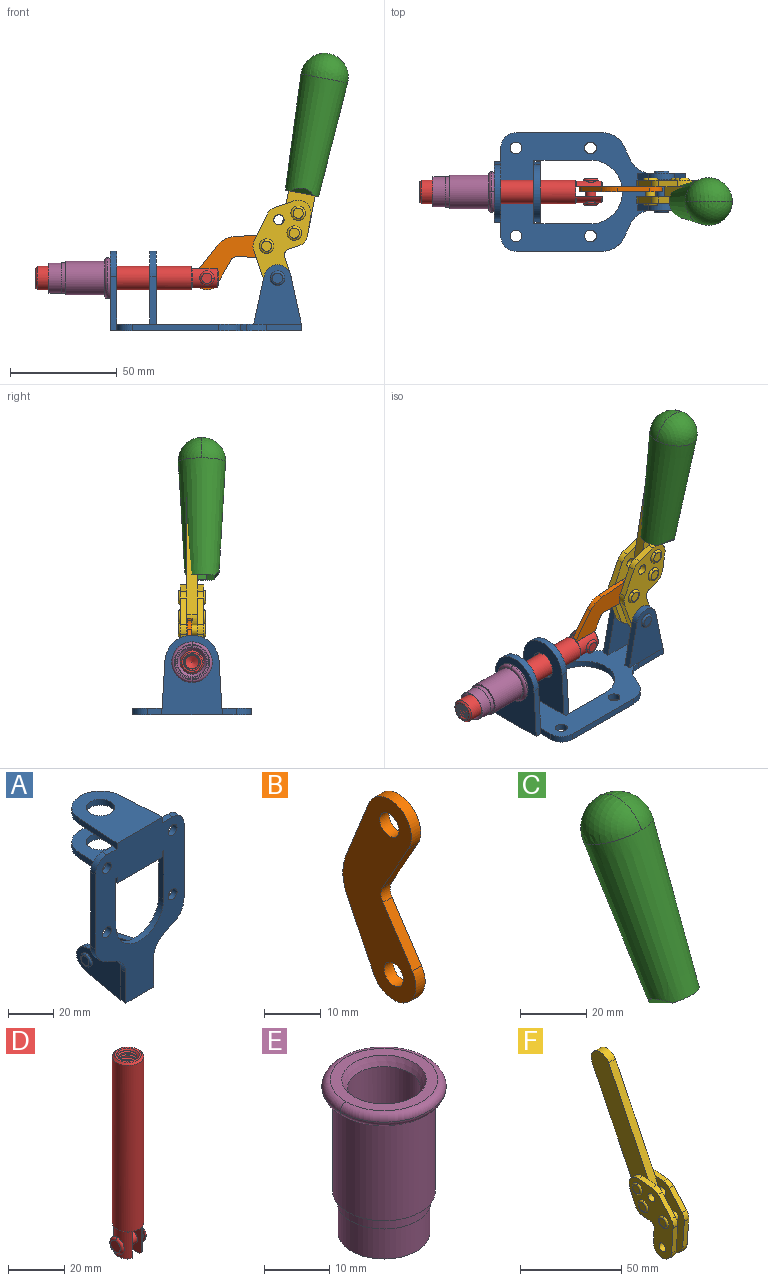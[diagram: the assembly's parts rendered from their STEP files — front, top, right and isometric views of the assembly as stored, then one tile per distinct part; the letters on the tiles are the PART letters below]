
ASSEMBLY  parts=6 mates=6
PART A: 55 faces, bbox 55.7x37.4x89.8 mm
  f0: torus R=2.41mm, axis (-1,0,0), area 15mm2, adj f11,f15,f25
  f1: torus R=2.41mm, axis (-1,0,0), area 15mm2, adj f10,f12,f22
  f2: cylinder r=2.78mm len=5.56mm, axis (0,-1,0), area 54.2mm2, adj f30,f54
  f3: cylinder r=14.99mm len=29.97mm, axis (0,-1,0), area 145.9mm2, adj f30,f49,f53,f54
  f4: cylinder r=2.78mm len=5.56mm, axis (0,-1,0), area 54.2mm2, adj f30,f54
  f5: cylinder r=2.78mm len=5.56mm, axis (0,-1,0), area 54.2mm2, adj f30,f54
  f6: cylinder r=2.78mm len=5.56mm, axis (0,-1,0), area 54.2mm2, adj f30,f54
  f7: cylinder r=6.35mm len=12.7mm, axis (0,0,1), area 123.6mm2, adj f27,f51
  f8: cylinder r=6.35mm len=12.7mm, axis (0,0,-1), area 124.7mm2, adj f21,f35
  f9: cylinder r=2.41mm len=11.18mm, axis (-1,0,0), area 169.4mm2, adj f16,f19
  f10: plane 4.83x4.83mm, normal (1,0,0), area 18.3mm2, adj f1,f12
  f11: plane 4.83x4.83mm, normal (-1,0,0), area 18.3mm2, adj f0,f15
  f12: torus R=2.41mm, axis (-1,0,0), area 15mm2, adj f1,f10,f22
  f13: cylinder r=6.35mm len=12.41mm, axis (1,0,0), area 53.4mm2, adj f18,f19,f22,f23
  f14: cylinder r=6.35mm len=12.41mm, axis (-1,0,0), area 53.4mm2, adj f16,f17,f24,f25
  f15: torus R=2.41mm, axis (-1,0,0), area 15mm2, adj f0,f11,f25
  f16: plane 27.86x22.35mm, normal (1,0,0), area 425.4mm2, adj f9,f14,f17,f24,f30
  f17: plane 22.86x4.97mm, normal (0,0.21,0.98), area 72.5mm2, adj f14,f16,f25,f30
  f18: plane 22.86x4.97mm, normal (0,0.21,0.98), area 72.5mm2, adj f13,f19,f22,f30
  f19: plane 27.86x22.35mm, normal (-1,0,0), area 425.4mm2, adj f9,f13,f18,f23,f30
  f20: cylinder r=12.7mm len=25.35mm, axis (0,0,-1), area 119.8mm2, adj f21,f34,f35,f36
  f21: plane 34.21x28.07mm, normal (0,0,-1), area 702.4mm2, adj f8,f20,f30,f34,f36
  f22: plane 27.96x22.45mm, normal (1,0,0), area 407.2mm2, adj f1,f12,f13,f18,f23,f30,f42,f43
  f23: plane 22.86x4.97mm, normal (0,0.21,-0.98), area 72.5mm2, adj f13,f19,f22,f44
  f24: plane 22.86x4.97mm, normal (0,0.21,-0.98), area 72.5mm2, adj f14,f16,f25,f44
  f25: plane 27.86x22.35mm, normal (-1,0,0), area 407.1mm2, adj f0,f14,f15,f17,f24,f30,f45,f46
  f26: plane 3.1x0.95mm, normal (0,0,-1), area 2.7mm2, adj f30,f49,f50,f54
  f27: plane 34.21x28.07mm, normal (0,0,1), area 702.4mm2, adj f7,f28,f30,f50,f52
  f28: cylinder r=12.7mm len=25.35mm, axis (0,0,1), area 118.8mm2, adj f27,f50,f51,f52
  f29: plane 3.1x0.95mm, normal (0,0,-1), area 2.7mm2, adj f30,f52,f53,f54
  f30: plane 86.54x55.63mm, normal (0,1,0), area 2362.9mm2, adj f2,f3,f4,f5,f6,f16,f17,f18
  f31: plane 40.56x3.1mm, normal (-1,0,0), area 125.7mm2, adj f30,f32,f48,f54
  f32: cylinder r=7.11mm len=7.11mm, axis (0,-1,0), area 34.6mm2, adj f30,f31,f33,f54
  f33: plane 6.67x3.1mm, normal (0,0,1), area 20.4mm2, adj f30,f32,f34,f54
  f34: plane 25.39x3.13mm, normal (-1,0.06,0), area 79.5mm2, adj f20,f21,f33,f35,f54
  f35: plane 37.31x28.45mm, normal (0,0,1), area 789.9mm2, adj f8,f20,f34,f36,f54
  f36: plane 25.39x3.13mm, normal (1,0.06,0), area 79.5mm2, adj f20,f21,f35,f37,f54
  f37: plane 6.67x3.1mm, normal (0,0,1), area 20.4mm2, adj f30,f36,f38,f54
  f38: cylinder r=7.11mm len=7.11mm, axis (0,-1,0), area 34.6mm2, adj f30,f37,f39,f54
  f39: plane 40.56x3.1mm, normal (1,0,0), area 125.7mm2, adj f30,f38,f40,f54
  f40: cylinder r=11.18mm len=10.16mm, axis (0,-1,0), area 39.5mm2, adj f30,f39,f41,f54
  f41: plane 6.09x3.1mm, normal (0.42,0,-0.91), area 20.8mm2, adj f30,f40,f42,f54
  f42: cylinder r=11.18mm len=9.41mm, axis (0,-1,0), area 37.2mm2, adj f22,f30,f41,f43,f54
  f43: plane 16.5x3.1mm, normal (1,0,0), area 51.1mm2, adj f22,f42,f44,f54
  f44: plane 17.37x3.1mm, normal (0,0,-1), area 53.8mm2, adj f23,f24,f30,f43,f45,f54
  f45: plane 16.5x3.1mm, normal (-1,0,0), area 51.1mm2, adj f25,f44,f46,f54
  f46: cylinder r=11.18mm len=9.41mm, axis (0,-1,0), area 37.2mm2, adj f25,f30,f45,f47,f54
  f47: plane 6.09x3.1mm, normal (-0.42,0,-0.91), area 20.8mm2, adj f30,f46,f48,f54
  f48: cylinder r=11.18mm len=10.16mm, axis (0,-1,0), area 39.5mm2, adj f30,f31,f47,f54
  f49: plane 26.54x3.1mm, normal (-1,0,0), area 82.3mm2, adj f3,f26,f30,f54
  f50: plane 25.39x3.1mm, normal (1,0.06,0), area 78.8mm2, adj f26,f27,f28,f51,f54
  f51: plane 37.31x28.45mm, normal (0,0,-1), area 789.9mm2, adj f7,f28,f50,f52,f54
  f52: plane 25.39x3.1mm, normal (-1,0.06,0), area 78.8mm2, adj f27,f28,f29,f51,f54
  f53: plane 26.54x3.1mm, normal (1,0,0), area 82.3mm2, adj f3,f29,f30,f54
  f54: plane 89.66x55.63mm, normal (0,-1,0), area 2678.5mm2, adj f2,f3,f4,f5,f6,f26,f29,f31
PART B: 12 faces, bbox 2.3x18.2x42.8 mm
  f0: cylinder r=2.4mm len=4.8mm, axis (1,0,0), area 34.9mm2, adj f4,f11
  f1: cylinder r=10.41mm len=8.47mm, axis (1,0,0), area 20.2mm2, adj f4,f9,f10,f11
  f2: cylinder r=3.05mm len=3.16mm, axis (1,0,0), area 7.7mm2, adj f4,f6,f7,f11
  f3: cylinder r=2.4mm len=4.8mm, axis (1,0,0), area 34.9mm2, adj f4,f11
  f4: plane 42.81x18.23mm, normal (-1,0,0), area 414.1mm2, adj f0,f1,f2,f3,f5,f6,f7,f8
  f5: cylinder r=5.54mm len=10.67mm, axis (1,0,0), area 41.8mm2, adj f4,f6,f10,f11
  f6: plane 11.66x6.53mm, normal (0,-0.87,-0.49), area 30.9mm2, adj f2,f4,f5,f11
  f7: plane 11.17x7.33mm, normal (0,-0.84,0.55), area 30.9mm2, adj f2,f4,f8,f11
  f8: cylinder r=5.54mm len=10.51mm, axis (1,0,0), area 41.8mm2, adj f4,f7,f9,f11
  f9: plane 13.67x6.67mm, normal (0,0.9,-0.44), area 35.1mm2, adj f1,f4,f8,f11
  f10: plane 14.1x5.7mm, normal (0,0.93,0.37), area 35.1mm2, adj f1,f4,f5,f11
  f11: plane 42.81x18.23mm, normal (1,0,0), area 414.1mm2, adj f0,f1,f2,f3,f5,f6,f7,f8
PART C: 11 faces, bbox 22.3x42.6x64.5 mm
  f0: sphere r=11.13mm, area 411.4mm2, adj f1,f8
  f1: cone r=11.11mm half-angle=3.3deg, axis (0,0.44,0.9), area 3251.8mm2, adj f0,f7,f8,f9,f10
  f2: cylinder r=6.16mm len=11.7mm, axis (1,0,0), area 89.5mm2, adj f3,f4,f5,f6
  f3: plane 60.23x36.75mm, normal (-1,0,0), area 763.6mm2, adj f2,f4,f6,f10
  f4: plane 51.37x25.05mm, normal (0,0.9,-0.44), area 264.2mm2, adj f2,f3,f5,f10
  f5: plane 60.23x36.75mm, normal (1,0,0), area 763.6mm2, adj f2,f4,f6,f10
  f6: plane 51.37x25.05mm, normal (0,-0.9,0.44), area 264.2mm2, adj f2,f3,f5,f10
  f7: plane 9.95x5.95mm, normal (0.71,-0.31,-0.64), area 25.8mm2, adj f1,f10
  f8: sphere r=11.13mm, area 411.4mm2, adj f0,f1
  f9: plane 9.95x5.95mm, normal (-0.71,-0.31,-0.64), area 25.8mm2, adj f1,f10
  f10: plane 14.27x11.38mm, normal (0,-0.44,-0.9), area 106.7mm2, adj f1,f3,f4,f5,f6,f7,f9
PART D: 48 faces, bbox 12.6x11.1x86.1 mm
  f0: torus R=2.41mm, axis (-1,0,0), area 15mm2, adj f30,f32,f34
  f1: torus R=2.41mm, axis (-1,0,0), area 15mm2, adj f29,f31,f33
  f2: cylinder r=5.54mm len=72.39mm, axis (0,0,1), area 2518.5mm2, adj f3,f4,f42,f43
  f3: cone r=5.54mm half-angle=45deg, axis (0,0,1), area 7.6mm2, adj f2,f5,f41
  f4: cone r=5.54mm half-angle=45deg, axis (0,0,-1), area 34.9mm2, adj f2,f39
  f5: cylinder r=5.08mm len=11.48mm, axis (0,0,1), area 108.3mm2, adj f3,f7,f8,f41
  f6: cylinder r=2.41mm len=4.83mm, axis (-1,0,0), area 71.2mm2, adj f40,f41
  f7: cylinder r=2.41mm len=4.83mm, axis (-1,0,0), area 7.6mm2, adj f5,f34
  f8: cone r=5.08mm half-angle=45deg, axis (0,0,1), area 10.6mm2, adj f5,f37,f41
  f9: cone r=3.98mm half-angle=45deg, axis (0,0,1), area 17.6mm2, adj f27,f39,f45,f46,f47
  f10: cylinder r=2.41mm len=4.83mm, axis (-1,0,0), area 7.6mm2, adj f33,f38
  f11: cylinder r=3.2mm len=6.4mm, axis (0,0,1), area 78.4mm2, adj f12,f28,f44,f45,f47
  f12: cylinder r=3.2mm len=6.4mm, axis (0,0,1), area 10.5mm2, adj f11,f13,f45,f47
  f13: cylinder r=3.2mm len=6.4mm, axis (0,0,1), area 10.5mm2, adj f12,f14,f45,f47
  f14: cylinder r=3.2mm len=6.4mm, axis (0,0,1), area 10.5mm2, adj f13,f15,f45,f47
  f15: cylinder r=3.2mm len=6.4mm, axis (0,0,1), area 10.5mm2, adj f14,f16,f45,f47
  f16: cylinder r=3.2mm len=6.4mm, axis (0,0,1), area 10.5mm2, adj f15,f17,f45,f47
  f17: cylinder r=3.2mm len=6.4mm, axis (0,0,1), area 10.5mm2, adj f16,f18,f45,f47
  f18: cylinder r=3.2mm len=6.4mm, axis (0,0,1), area 10.5mm2, adj f17,f19,f45,f47
  f19: cylinder r=3.2mm len=6.4mm, axis (0,0,1), area 10.5mm2, adj f18,f20,f45,f47
  f20: cylinder r=3.2mm len=6.4mm, axis (0,0,1), area 10.5mm2, adj f19,f21,f45,f47
  f21: cylinder r=3.2mm len=6.4mm, axis (0,0,1), area 10.5mm2, adj f20,f22,f45,f47
  f22: cylinder r=3.2mm len=6.4mm, axis (0,0,1), area 10.5mm2, adj f21,f23,f45,f47
  f23: cylinder r=3.2mm len=6.4mm, axis (0,0,1), area 10.5mm2, adj f22,f24,f45,f47
  f24: cylinder r=3.2mm len=6.4mm, axis (0,0,1), area 10.5mm2, adj f23,f25,f45,f47
  f25: cylinder r=3.2mm len=6.4mm, axis (0,0,1), area 10.5mm2, adj f24,f26,f45,f47
  f26: cylinder r=3.2mm len=6.4mm, axis (0,0,1), area 10.5mm2, adj f25,f27,f45,f47
  f27: cylinder r=3.2mm len=6.4mm, axis (0,0,1), area 7.4mm2, adj f9,f26,f45,f47
  f28: cone r=3.2mm half-angle=60deg, axis (0,0,1), area 37.2mm2, adj f11
  f29: plane 4.83x4.83mm, normal (-1,0,0), area 18.3mm2, adj f1,f31
  f30: plane 4.83x4.83mm, normal (1,0,0), area 18.3mm2, adj f0,f32
  f31: torus R=2.41mm, axis (-1,0,0), area 15mm2, adj f1,f29,f33
  f32: torus R=2.41mm, axis (-1,0,0), area 15mm2, adj f0,f30,f34
  f33: plane 6.83x6.83mm, normal (1,0,0), area 18.3mm2, adj f1,f10,f31
  f34: plane 6.83x6.83mm, normal (-1,0,0), area 18.3mm2, adj f0,f7,f32
  f35: cone r=5.08mm half-angle=45deg, axis (0,0,1), area 10.6mm2, adj f36,f38,f40
  f36: plane 7.25x1.97mm, normal (0,0,-1), area 10mm2, adj f35,f40
  f37: plane 7.25x1.97mm, normal (0,0,-1), area 10mm2, adj f8,f41
  f38: cylinder r=5.08mm len=11.48mm, axis (0,0,1), area 108.3mm2, adj f10,f35,f40,f42
  f39: plane 9.55x9.55mm, normal (0,0,1), area 22mm2, adj f4,f9
  f40: plane 12.76x10.09mm, normal (1,0,0), area 95.7mm2, adj f6,f35,f36,f38,f42,f43
  f41: plane 12.76x10.09mm, normal (-1,0,0), area 95.7mm2, adj f3,f5,f6,f8,f37,f43
  f42: cone r=5.54mm half-angle=45deg, axis (0,0,1), area 7.6mm2, adj f2,f38,f40
  f43: plane 11.07x4.7mm, normal (0,0,-1), area 50.4mm2, adj f2,f40,f41
  f44: plane 0.89x0.62mm, normal (-1,0,0), area 0.3mm2, adj f11,f45,f46,f47
  f45: bspline ~24.8x7.63mm, area 266.6mm2, adj f9,f11,f12,f13,f14,f15,f16,f17
  f46: bspline ~24.87x7.63mm, area 73.6mm2, adj f9,f44,f45,f47
  f47: bspline ~24.98x7.63mm, area 272.5mm2, adj f9,f11,f12,f13,f14,f15,f16,f17
PART E: 15 faces, bbox 20.6x20.6x28.7 mm
  f0: torus R=8.26mm, axis (0,0,1), area 56.8mm2, adj f1,f10,f12
  f1: torus R=8.26mm, axis (0,0,1), area 56.8mm2, adj f0,f6,f13
  f2: cylinder r=5.59mm len=25.91mm, axis (0,0,1), area 909.6mm2, adj f3,f4
  f3: cone r=6.86mm half-angle=45deg, axis (0,0,-1), area 70.2mm2, adj f2,f14
  f4: cone r=6.47mm half-angle=30deg, axis (0,0,1), area 66.7mm2, adj f2,f13
  f5: cylinder r=7.04mm len=14.07mm, axis (0,0,1), area 252.6mm2, adj f11,f14
  f6: torus R=8.26mm, axis (0,0,1), area 56.8mm2, adj f1,f12,f13
  f7: cylinder r=7.16mm len=14.33mm, axis (0,0,1), area 91.5mm2, adj f9,f11
  f8: cylinder r=7.86mm len=18.42mm, axis (0,0,1), area 909.6mm2, adj f9,f10
  f9: plane 15.72x15.72mm, normal (0,0,-1), area 33mm2, adj f7,f8
  f10: plane 16.51x16.51mm, normal (0,0,-1), area 19.9mm2, adj f0,f8,f12
  f11: plane 14.33x14.33mm, normal (0,0,-1), area 5.7mm2, adj f5,f7
  f12: torus R=8.26mm, axis (0,0,1), area 56.8mm2, adj f0,f6,f10
  f13: plane 16.51x16.51mm, normal (0,0,1), area 82.7mm2, adj f1,f4,f6
  f14: plane 14.07x14.07mm, normal (0,0,-1), area 7.8mm2, adj f3,f5
PART F: 59 faces, bbox 12.9x60.2x99.6 mm
  f0: torus R=2.39mm, axis (-1,0,0), area 14.9mm2, adj f20,f43,f51
  f1: torus R=2.39mm, axis (-1,0,0), area 14.9mm2, adj f19,f42,f51
  f2: torus R=2.39mm, axis (-1,0,0), area 14.9mm2, adj f18,f35,f51
  f3: torus R=2.39mm, axis (-1,0,0), area 14.9mm2, adj f14,f17,f23
  f4: torus R=2.39mm, axis (-1,0,0), area 14.9mm2, adj f13,f16,f23
  f5: torus R=2.39mm, axis (-1,0,0), area 14.9mm2, adj f12,f15,f23
  f6: cylinder r=2.39mm len=4.78mm, axis (1,0,0), area 46.5mm2, adj f48,f50,f51
  f7: cylinder r=2.39mm len=4.78mm, axis (1,0,0), area 46.5mm2, adj f50,f51
  f8: cylinder r=6.35mm len=12.68mm, axis (1,0,0), area 61.8mm2, adj f38,f39,f50,f51
  f9: cylinder r=2.39mm len=4.78mm, axis (-1,0,0), area 70.5mm2, adj f46,f50
  f10: cylinder r=2.39mm len=4.78mm, axis (-1,0,0), area 46.5mm2, adj f23,f45,f46
  f11: cylinder r=2.39mm len=4.78mm, axis (-1,0,0), area 46.5mm2, adj f23,f46
  f12: plane 4.78x4.78mm, normal (1,0,0), area 17.9mm2, adj f5,f15
  f13: plane 4.78x4.78mm, normal (1,0,0), area 17.9mm2, adj f4,f16
  f14: plane 4.78x4.78mm, normal (1,0,0), area 17.9mm2, adj f3,f17
  f15: torus R=2.39mm, axis (-1,0,0), area 14.9mm2, adj f5,f12,f23
  f16: torus R=2.39mm, axis (-1,0,0), area 14.9mm2, adj f4,f13,f23
  f17: torus R=2.39mm, axis (-1,0,0), area 14.9mm2, adj f3,f14,f23
  f18: plane 4.78x4.78mm, normal (-1,0,0), area 17.9mm2, adj f2,f35
  f19: plane 4.78x4.78mm, normal (-1,0,0), area 17.9mm2, adj f1,f42
  f20: plane 4.78x4.78mm, normal (-1,0,0), area 17.9mm2, adj f0,f43
  f21: plane 2.26x0.2mm, normal (1,0,0), area 0.2mm2, adj f31,f44
  f22: plane 2.26x0.2mm, normal (-1,0,0), area 0.2mm2, adj f41,f44
  f23: plane 39.37x30.77mm, normal (1,0,0), area 565.5mm2, adj f3,f4,f5,f10,f11,f15,f16,f17
  f24: cylinder r=6.1mm len=4.15mm, axis (-1,0,0), area 14.7mm2, adj f23,f25,f32,f46
  f25: plane 10.25x9.01mm, normal (0,-0.75,0.66), area 42.3mm2, adj f23,f24,f26,f46
  f26: cylinder r=6.35mm len=4.64mm, axis (-1,0,0), area 15.6mm2, adj f23,f25,f27,f46
  f27: plane 15.84x3.1mm, normal (0,-1,-0.07), area 49.2mm2, adj f23,f26,f28,f46
  f28: cylinder r=6.35mm len=12.68mm, axis (-1,0,0), area 61.8mm2, adj f23,f27,f29,f46
  f29: plane 8.11x3.1mm, normal (0,1,0.07), area 25.2mm2, adj f23,f28,f30,f46
  f30: cylinder r=3.05mm len=3.25mm, axis (-1,0,0), area 14.8mm2, adj f23,f29,f31,f46
  f31: plane 5.99x3.1mm, normal (0,0.07,-1), area 18.6mm2, adj f21,f23,f30,f44,f46
  f32: plane 9.5x3.1mm, normal (0,-0.07,1), area 29.5mm2, adj f23,f24,f33,f46,f47
  f33: cylinder r=6.1mm len=8.63mm, axis (-1,0,0), area 39.1mm2, adj f23,f32,f34,f47
  f34: plane 8.65x3.96mm, normal (0,0.91,-0.42), area 29.5mm2, adj f23,f33,f44,f47
  f35: torus R=2.39mm, axis (-1,0,0), area 14.9mm2, adj f2,f18,f51
  f36: plane 10.25x9.01mm, normal (0,-0.75,0.66), area 42.3mm2, adj f37,f49,f50,f51
  f37: cylinder r=6.35mm len=4.64mm, axis (1,0,0), area 15.6mm2, adj f36,f38,f50,f51
  f38: plane 15.84x3.1mm, normal (0,-1,-0.07), area 49.2mm2, adj f8,f37,f50,f51
  f39: plane 8.11x3.1mm, normal (0,1,0.07), area 25.2mm2, adj f8,f40,f50,f51
  f40: cylinder r=3.05mm len=3.25mm, axis (1,0,0), area 14.8mm2, adj f39,f41,f50,f51
  f41: plane 5.99x3.1mm, normal (0,0.07,-1), area 18.6mm2, adj f22,f40,f44,f50,f51
  f42: torus R=2.39mm, axis (-1,0,0), area 14.9mm2, adj f1,f19,f51
  f43: torus R=2.39mm, axis (-1,0,0), area 14.9mm2, adj f0,f20,f51
  f44: cylinder r=6.35mm len=12.12mm, axis (-1,0,0), area 128.9mm2, adj f21,f22,f23,f31,f34,f41,f46,f47
  f45: plane 2.65x1.35mm, normal (1,0,0), area 1mm2, adj f10,f55
  f46: plane 39.08x20.42mm, normal (-1,0,0), area 412.5mm2, adj f9,f10,f11,f24,f25,f26,f27,f28
  f47: plane 77.62x39.82mm, normal (1,0,0), area 850mm2, adj f32,f33,f34,f44,f53,f54,f55
  f48: plane 2.65x1.35mm, normal (-1,0,0), area 1mm2, adj f6,f55
  f49: cylinder r=6.1mm len=4.15mm, axis (1,0,0), area 14.7mm2, adj f36,f50,f51,f56
  f50: plane 39.08x20.42mm, normal (1,0,0), area 412.5mm2, adj f6,f7,f8,f9,f36,f37,f38,f39
  f51: plane 39.37x30.77mm, normal (-1,0,0), area 565.5mm2, adj f0,f1,f2,f6,f7,f8,f35,f36
  f52: plane 8.65x3.96mm, normal (0,0.91,-0.42), area 29.5mm2, adj f44,f51,f57,f58
  f53: plane 68.49x33.4mm, normal (0,0.9,-0.44), area 358.1mm2, adj f44,f47,f54,f58
  f54: cylinder r=6.35mm len=12.06mm, axis (1,0,0), area 93.7mm2, adj f47,f53,f55,f58
  f55: plane 68.49x33.4mm, normal (0,-0.9,0.44), area 358.1mm2, adj f44,f45,f46,f47,f48,f50,f54,f58
  f56: plane 9.5x3.1mm, normal (0,-0.07,1), area 29.5mm2, adj f49,f50,f51,f57,f58
  f57: cylinder r=6.1mm len=8.63mm, axis (1,0,0), area 39.1mm2, adj f51,f52,f56,f58
  f58: plane 77.62x39.82mm, normal (-1,0,0), area 850mm2, adj f44,f52,f53,f54,f55,f56,f57
PLACE A rot(axis=(0.58,-0.58,-0.58),120deg) t=(0,0,0)mm fixed
PLACE B rot(axis=(0.47,0.47,0.75),106.2deg) t=(23.91,1.16,10.71)mm
PLACE C rot(axis=(0.13,-0.13,-0.98),91deg) t=(0.01,-4.66,49.24)mm
PLACE D rot(axis=(0.58,-0.58,-0.58),120deg) t=(14.42,0,0)mm
PLACE E rot(axis=(0,1,0),90deg) t=(-95.33,-24.61,24.61)mm
PLACE F rot(axis=(0.13,-0.13,-0.98),91deg) t=(0.01,0,49.24)mm
MATE revolute B.f3 <-> D.f6  axis (0,1,0) through (-1.05,0,24.61)mm
MATE slider D.f2 <-> E.f2  axis (-1,0,0) through (-44.36,0,24.61)mm
MATE fastened C.f2 <-> F.f54  axis (0,-1,0) through (54.46,-2.35,120.54)mm
MATE revolute B.f0 <-> F.f4  axis (0,1,0) through (26.92,0,39.62)mm
MATE revolute A.f0 <-> F.f7  axis (0,1,0) through (32.09,0,24.61)mm
MATE fastened A.f7 <-> E.f2  axis (-1,0,0) through (-46.39,0,24.61)mm
